# Revit family: Ceiling Tiles - Tegular and Square
name_source: partatom
category: Specialty Equipment
units: mm (PartAtom-declared; Revit-internal decimal feet)

## family parameters
Always vertical = No
Cut with Voids When Loaded = No
Enable Cutting in Views = Yes
Maintain Annotation Orientation = No
OmniClass Number = 23.35.00.00
OmniClass Title = Covering, Cladding, and Finishes
Part Type = Normal
Room Calculation Point = No
Round Connector Dimension = Use Diameter
Shared = No
Work Plane-Based = Yes

## types (168) — shared parameters
Acoustics - NRC = Sound absorption varies from NRC 0.45 to 0.95 based on installation method used when tested per ASTM C423.
Assembly Code = C30
Default Elevation = 4' - 0"
Description = Acoustic Panels
Fire Rating = ASTM E84 - Class A
Manufacturer = Acoustical Surfaces, Inc.
Material = Envirocoustic Wood Wool
Model = Envirocoustic Wood Wool
Recycled Content Percentage = 0%
Type Comments = Acoustic Panels
URL = https://www.acousticalsurfaces.com
Width = 2' - 0"

## per-type parameters (varying)
| type | A | Backer | Backer Options | Backer Thickness | Edge Option | Finish | Length | T | Thickness Options | ‍      0. SoundTex Backer | ‍      0. Thickness 5/8" (only for Square edge) | ‍      1. 1" CFAB Backer | ‍      1. Thickness 1" | ‍      2. 2" CFAB Backer | ‍      2. Thickness 1-3/8" | ‍      3. Thickness 2" | ‍     1. Tegular | ‍     2. Square |
| 2" Square 2x4 Custom Painted With 2” CFAB Backer | 0' - 2" | Yes | 2 | 0' - 2" | 2 | Paint - Acoustical-Surfaces - Custom Painted | 4' - 0" | 0' - 2" | 3 | No | No | No | No | Yes | No | Yes | No | Yes |
| 2" Square 2x2 Custom Painted With 2” CFAB Backer | 0' - 2" | Yes | 2 | 0' - 2" | 2 | Paint - Acoustical-Surfaces - Custom Painted | 2' - 0" | 0' - 2" | 3 | No | No | No | No | Yes | No | Yes | No | Yes |
| 2" Square 2x4 Custom Painted With 1” CFAB Backer | 0' - 1" | Yes | 1 | 0' - 1" | 2 | Paint - Acoustical-Surfaces - Custom Painted | 4' - 0" | 0' - 2" | 3 | No | No | Yes | No | No | No | Yes | No | Yes |
| 2" Square 2x2 Custom Painted With 1” CFAB Backer | 0' - 1" | Yes | 1 | 0' - 1" | 2 | Paint - Acoustical-Surfaces - Custom Painted | 2' - 0" | 0' - 2" | 3 | No | No | Yes | No | No | No | Yes | No | Yes |
| 2" Square 2x4 Custom Painted With Backer 1/16" | 0' - 0" | Yes | 0 | 0' - 0" | 2 | Paint - Acoustical-Surfaces - Custom Painted | 4' - 0" | 0' - 2" | 3 | Yes | No | No | No | No | No | Yes | No | Yes |
| 2" Square 2x2 Custom Painted With Backer 1/16" | 0' - 0" | Yes | 0 | 0' - 0" | 2 | Paint - Acoustical-Surfaces - Custom Painted | 2' - 0" | 0' - 2" | 3 | Yes | No | No | No | No | No | Yes | No | Yes |
| 2" Square 2x4 Custom Painted | 0' - 0" | No | 0 | 0' - 0" | 2 | Paint - Acoustical-Surfaces - Custom Painted | 4' - 0" | 0' - 2" | 3 | Yes | No | No | No | No | No | Yes | No | Yes |
| 2" Square 2x2 Custom Painted | 0' - 0" | No | 0 | 0' - 0" | 2 | Paint - Acoustical-Surfaces - Custom Painted | 2' - 0" | 0' - 2" | 3 | Yes | No | No | No | No | No | Yes | No | Yes |
| 2" Square 2x4 Primed White With 2” CFAB Backer | 0' - 2" | Yes | 2 | 0' - 2" | 2 | Paint - Acoustical-Surfaces - Primed White | 4' - 0" | 0' - 2" | 3 | No | No | No | No | Yes | No | Yes | No | Yes |
| 2" Square 2x2 Primed White With 2” CFAB Backer | 0' - 2" | Yes | 2 | 0' - 2" | 2 | Paint - Acoustical-Surfaces - Primed White | 2' - 0" | 0' - 2" | 3 | No | No | No | No | Yes | No | Yes | No | Yes |
| 2" Square 2x4 Primed White With 1” CFAB Backer | 0' - 1" | Yes | 1 | 0' - 1" | 2 | Paint - Acoustical-Surfaces - Primed White | 4' - 0" | 0' - 2" | 3 | No | No | Yes | No | No | No | Yes | No | Yes |
| 2" Square 2x2 Primed White With 1” CFAB Backer | 0' - 1" | Yes | 1 | 0' - 1" | 2 | Paint - Acoustical-Surfaces - Primed White | 2' - 0" | 0' - 2" | 3 | No | No | Yes | No | No | No | Yes | No | Yes |
| 2" Square 2x4 Primed White With Backer 1/16" | 0' - 0" | Yes | 0 | 0' - 0" | 2 | Paint - Acoustical-Surfaces - Primed White | 4' - 0" | 0' - 2" | 3 | Yes | No | No | No | No | No | Yes | No | Yes |
| 2" Square 2x2 Primed White With Backer 1/16" | 0' - 0" | Yes | 0 | 0' - 0" | 2 | Paint - Acoustical-Surfaces - Primed White | 2' - 0" | 0' - 2" | 3 | Yes | No | No | No | No | No | Yes | No | Yes |
| 2" Square 2x4 Primed White | 0' - 0" | No | 0 | 0' - 0" | 2 | Paint - Acoustical-Surfaces - Primed White | 4' - 0" | 0' - 2" | 3 | Yes | No | No | No | No | No | Yes | No | Yes |
| 2" Square 2x2 Primed White | 0' - 0" | No | 0 | 0' - 0" | 2 | Paint - Acoustical-Surfaces - Primed White | 2' - 0" | 0' - 2" | 3 | Yes | No | No | No | No | No | Yes | No | Yes |
| 2" Square 2x4 Primed Clear With 2” CFAB Backer | 0' - 2" | Yes | 2 | 0' - 2" | 2 | Paint - Acoustical-Surfaces - Primed Clear | 4' - 0" | 0' - 2" | 3 | No | No | No | No | Yes | No | Yes | No | Yes |
| 2" Square 2x2 Primed Clear With 2” CFAB Backer | 0' - 2" | Yes | 2 | 0' - 2" | 2 | Paint - Acoustical-Surfaces - Primed Clear | 2' - 0" | 0' - 2" | 3 | No | No | No | No | Yes | No | Yes | No | Yes |
| 2" Square 2x4 Primed Clear With 1” CFAB Backer | 0' - 1" | Yes | 1 | 0' - 1" | 2 | Paint - Acoustical-Surfaces - Primed Clear | 4' - 0" | 0' - 2" | 3 | No | No | Yes | No | No | No | Yes | No | Yes |
| 2" Square 2x2 Primed Clear With 1” CFAB Backer | 0' - 1" | Yes | 1 | 0' - 1" | 2 | Paint - Acoustical-Surfaces - Primed Clear | 2' - 0" | 0' - 2" | 3 | No | No | Yes | No | No | No | Yes | No | Yes |
| 2" Square 2x4 Primed Clear With Backer 1/16" | 0' - 0" | Yes | 0 | 0' - 0" | 2 | Paint - Acoustical-Surfaces - Primed Clear | 4' - 0" | 0' - 2" | 3 | Yes | No | No | No | No | No | Yes | No | Yes |
| 2" Square 2x2 Primed Clear With Backer 1/16" | 0' - 0" | Yes | 0 | 0' - 0" | 2 | Paint - Acoustical-Surfaces - Primed Clear | 2' - 0" | 0' - 2" | 3 | Yes | No | No | No | No | No | Yes | No | Yes |
| 2" Square 2x4 Primed Clear | 0' - 0" | No | 0 | 0' - 0" | 2 | Paint - Acoustical-Surfaces - Primed Clear | 4' - 0" | 0' - 2" | 3 | Yes | No | No | No | No | No | Yes | No | Yes |
| 2" Square 2x2 Primed Clear | 0' - 0" | No | 0 | 0' - 0" | 2 | Paint - Acoustical-Surfaces - Primed Clear | 2' - 0" | 0' - 2" | 3 | Yes | No | No | No | No | No | Yes | No | Yes |
| 1-3/8" Square 2x4 Custom Painted With 2” CFAB Backer | 0' - 2" | Yes | 2 | 0' - 2" | 2 | Paint - Acoustical-Surfaces - Custom Painted | 4' - 0" | 0' - 1 1/2" | 2 | No | No | No | No | Yes | Yes | No | No | Yes |
| 1-3/8" Square 2x2 Custom Painted With 2” CFAB Backer | 0' - 2" | Yes | 2 | 0' - 2" | 2 | Paint - Acoustical-Surfaces - Custom Painted | 2' - 0" | 0' - 1 1/2" | 2 | No | No | No | No | Yes | Yes | No | No | Yes |
| 1-3/8" Square 2x4 Custom Painted With 1” CFAB Backer | 0' - 1" | Yes | 1 | 0' - 1" | 2 | Paint - Acoustical-Surfaces - Custom Painted | 4' - 0" | 0' - 1 1/2" | 2 | No | No | Yes | No | No | Yes | No | No | Yes |
| 1-3/8" Square 2x2 Custom Painted With 1” CFAB Backer | 0' - 1" | Yes | 1 | 0' - 1" | 2 | Paint - Acoustical-Surfaces - Custom Painted | 2' - 0" | 0' - 1 1/2" | 2 | No | No | Yes | No | No | Yes | No | No | Yes |
| 1-3/8" Square 2x4 Custom Painted With Backer 1/16" | 0' - 0" | Yes | 0 | 0' - 0" | 2 | Paint - Acoustical-Surfaces - Custom Painted | 4' - 0" | 0' - 1 1/2" | 2 | Yes | No | No | No | No | Yes | No | No | Yes |
| 1-3/8" Square 2x2 Custom Painted With Backer 1/16" | 0' - 0" | Yes | 0 | 0' - 0" | 2 | Paint - Acoustical-Surfaces - Custom Painted | 2' - 0" | 0' - 1 1/2" | 2 | Yes | No | No | No | No | Yes | No | No | Yes |
| 1-3/8" Square 2x4 Custom Painted | 0' - 0" | No | 0 | 0' - 0" | 2 | Paint - Acoustical-Surfaces - Custom Painted | 4' - 0" | 0' - 1 1/2" | 2 | Yes | No | No | No | No | Yes | No | No | Yes |
| 1-3/8" Square 2x2 Custom Painted | 0' - 0" | No | 0 | 0' - 0" | 2 | Paint - Acoustical-Surfaces - Custom Painted | 2' - 0" | 0' - 1 1/2" | 2 | Yes | No | No | No | No | Yes | No | No | Yes |
| 1-3/8" Square 2x4 Primed White With 2” CFAB Backer | 0' - 2" | Yes | 2 | 0' - 2" | 2 | Paint - Acoustical-Surfaces - Primed White | 4' - 0" | 0' - 1 1/2" | 2 | No | No | No | No | Yes | Yes | No | No | Yes |
| 1-3/8" Square 2x2 Primed White With 2” CFAB Backer | 0' - 2" | Yes | 2 | 0' - 2" | 2 | Paint - Acoustical-Surfaces - Primed White | 2' - 0" | 0' - 1 1/2" | 2 | No | No | No | No | Yes | Yes | No | No | Yes |
| 1-3/8" Square 2x4 Primed White With 1” CFAB Backer | 0' - 1" | Yes | 1 | 0' - 1" | 2 | Paint - Acoustical-Surfaces - Primed White | 4' - 0" | 0' - 1 1/2" | 2 | No | No | Yes | No | No | Yes | No | No | Yes |
| 1-3/8" Square 2x2 Primed White With 1” CFAB Backer | 0' - 1" | Yes | 1 | 0' - 1" | 2 | Paint - Acoustical-Surfaces - Primed White | 2' - 0" | 0' - 1 1/2" | 2 | No | No | Yes | No | No | Yes | No | No | Yes |
| 1-3/8" Square 2x4 Primed White With Backer 1/16" | 0' - 0" | Yes | 0 | 0' - 0" | 2 | Paint - Acoustical-Surfaces - Primed White | 4' - 0" | 0' - 1 1/2" | 2 | Yes | No | No | No | No | Yes | No | No | Yes |
| 1-3/8" Square 2x2 Primed White With Backer 1/16" | 0' - 0" | Yes | 0 | 0' - 0" | 2 | Paint - Acoustical-Surfaces - Primed White | 2' - 0" | 0' - 1 1/2" | 2 | Yes | No | No | No | No | Yes | No | No | Yes |
| 1-3/8" Square 2x4 Primed White | 0' - 0" | No | 0 | 0' - 0" | 2 | Paint - Acoustical-Surfaces - Primed White | 4' - 0" | 0' - 1 1/2" | 2 | Yes | No | No | No | No | Yes | No | No | Yes |
| 1-3/8" Square 2x2 Primed White | 0' - 0" | No | 0 | 0' - 0" | 2 | Paint - Acoustical-Surfaces - Primed White | 2' - 0" | 0' - 1 1/2" | 2 | Yes | No | No | No | No | Yes | No | No | Yes |
| 1-3/8" Square 2x4 Primed Clear With 2” CFAB Backer | 0' - 2" | Yes | 2 | 0' - 2" | 2 | Paint - Acoustical-Surfaces - Primed Clear | 4' - 0" | 0' - 1 1/2" | 2 | No | No | No | No | Yes | Yes | No | No | Yes |
| 1-3/8" Square 2x2 Primed Clear With 2” CFAB Backer | 0' - 2" | Yes | 2 | 0' - 2" | 2 | Paint - Acoustical-Surfaces - Primed Clear | 2' - 0" | 0' - 1 1/2" | 2 | No | No | No | No | Yes | Yes | No | No | Yes |
| 1-3/8" Square 2x4 Primed Clear With 1” CFAB Backer | 0' - 1" | Yes | 1 | 0' - 1" | 2 | Paint - Acoustical-Surfaces - Primed Clear | 4' - 0" | 0' - 1 1/2" | 2 | No | No | Yes | No | No | Yes | No | No | Yes |
| 1-3/8" Square 2x2 Primed Clear With 1” CFAB Backer | 0' - 1" | Yes | 1 | 0' - 1" | 2 | Paint - Acoustical-Surfaces - Primed Clear | 2' - 0" | 0' - 1 1/2" | 2 | No | No | Yes | No | No | Yes | No | No | Yes |
| 1-3/8" Square 2x4 Primed Clear With Backer 1/16" | 0' - 0" | Yes | 0 | 0' - 0" | 2 | Paint - Acoustical-Surfaces - Primed Clear | 4' - 0" | 0' - 1 1/2" | 2 | Yes | No | No | No | No | Yes | No | No | Yes |
| 1-3/8" Square 2x2 Primed Clear With Backer 1/16" | 0' - 0" | Yes | 0 | 0' - 0" | 2 | Paint - Acoustical-Surfaces - Primed Clear | 2' - 0" | 0' - 1 1/2" | 2 | Yes | No | No | No | No | Yes | No | No | Yes |
| 1-3/8" Square 2x4 Primed Clear | 0' - 0" | No | 0 | 0' - 0" | 2 | Paint - Acoustical-Surfaces - Primed Clear | 4' - 0" | 0' - 1 1/2" | 2 | Yes | No | No | No | No | Yes | No | No | Yes |
| 1-3/8" Square 2x2 Primed Clear | 0' - 0" | No | 0 | 0' - 0" | 2 | Paint - Acoustical-Surfaces - Primed Clear | 2' - 0" | 0' - 1 1/2" | 2 | Yes | No | No | No | No | Yes | No | No | Yes |
| 1" Square 2x4 Custom Painted With 2” CFAB Backer | 0' - 2" | Yes | 2 | 0' - 2" | 2 | Paint - Acoustical-Surfaces - Custom Painted | 4' - 0" | 0' - 1" | 1 | No | No | No | Yes | Yes | No | No | No | Yes |
| 1" Square 2x2 Custom Painted With 2” CFAB Backer | 0' - 2" | Yes | 2 | 0' - 2" | 2 | Paint - Acoustical-Surfaces - Custom Painted | 2' - 0" | 0' - 1" | 1 | No | No | No | Yes | Yes | No | No | No | Yes |
| 1" Square 2x4 Custom Painted With 1” CFAB Backer | 0' - 1" | Yes | 1 | 0' - 1" | 2 | Paint - Acoustical-Surfaces - Custom Painted | 4' - 0" | 0' - 1" | 1 | No | No | Yes | Yes | No | No | No | No | Yes |
| 1" Square 2x2 Custom Painted With 1” CFAB Backer | 0' - 1" | Yes | 1 | 0' - 1" | 2 | Paint - Acoustical-Surfaces - Custom Painted | 2' - 0" | 0' - 1" | 1 | No | No | Yes | Yes | No | No | No | No | Yes |
| 1" Square 2x4 Custom Painted With Backer 1/16" | 0' - 0" | Yes | 0 | 0' - 0" | 2 | Paint - Acoustical-Surfaces - Custom Painted | 4' - 0" | 0' - 1" | 1 | Yes | No | No | Yes | No | No | No | No | Yes |
| 1" Square 2x2 Custom Painted With Backer 1/16" | 0' - 0" | Yes | 0 | 0' - 0" | 2 | Paint - Acoustical-Surfaces - Custom Painted | 2' - 0" | 0' - 1" | 1 | Yes | No | No | Yes | No | No | No | No | Yes |
| 1" Square 2x4 Custom Painted | 0' - 0" | No | 0 | 0' - 0" | 2 | Paint - Acoustical-Surfaces - Custom Painted | 4' - 0" | 0' - 1" | 1 | Yes | No | No | Yes | No | No | No | No | Yes |
| 1" Square 2x2 Custom Painted | 0' - 0" | No | 0 | 0' - 0" | 2 | Paint - Acoustical-Surfaces - Custom Painted | 2' - 0" | 0' - 1" | 1 | Yes | No | No | Yes | No | No | No | No | Yes |
| 1" Square 2x4 Primed White With 2” CFAB Backer | 0' - 2" | Yes | 2 | 0' - 2" | 2 | Paint - Acoustical-Surfaces - Primed White | 4' - 0" | 0' - 1" | 1 | No | No | No | Yes | Yes | No | No | No | Yes |
| 1" Square 2x2 Primed White With 2” CFAB Backer | 0' - 2" | Yes | 2 | 0' - 2" | 2 | Paint - Acoustical-Surfaces - Primed White | 2' - 0" | 0' - 1" | 1 | No | No | No | Yes | Yes | No | No | No | Yes |
| 1" Square 2x4 Primed White With 1” CFAB Backer | 0' - 1" | Yes | 1 | 0' - 1" | 2 | Paint - Acoustical-Surfaces - Primed White | 4' - 0" | 0' - 1" | 1 | No | No | Yes | Yes | No | No | No | No | Yes |
| 1" Square 2x2 Primed White With 1” CFAB Backer | 0' - 1" | Yes | 1 | 0' - 1" | 2 | Paint - Acoustical-Surfaces - Primed White | 2' - 0" | 0' - 1" | 1 | No | No | Yes | Yes | No | No | No | No | Yes |
| 1" Square 2x4 Primed White With Backer 1/16" | 0' - 0" | Yes | 0 | 0' - 0" | 2 | Paint - Acoustical-Surfaces - Primed White | 4' - 0" | 0' - 1" | 1 | Yes | No | No | Yes | No | No | No | No | Yes |
| 1" Square 2x2 Primed White With Backer 1/16" | 0' - 0" | Yes | 0 | 0' - 0" | 2 | Paint - Acoustical-Surfaces - Primed White | 2' - 0" | 0' - 1" | 1 | Yes | No | No | Yes | No | No | No | No | Yes |
| 1" Square 2x4 Primed White | 0' - 0" | No | 0 | 0' - 0" | 2 | Paint - Acoustical-Surfaces - Primed White | 4' - 0" | 0' - 1" | 1 | Yes | No | No | Yes | No | No | No | No | Yes |
| 1" Square 2x2 Primed White | 0' - 0" | No | 0 | 0' - 0" | 2 | Paint - Acoustical-Surfaces - Primed White | 2' - 0" | 0' - 1" | 1 | Yes | No | No | Yes | No | No | No | No | Yes |
| 1" Square 2x4 Primed Clear With 2” CFAB Backer | 0' - 2" | Yes | 2 | 0' - 2" | 2 | Paint - Acoustical-Surfaces - Primed Clear | 4' - 0" | 0' - 1" | 1 | No | No | No | Yes | Yes | No | No | No | Yes |
| 1" Square 2x2 Primed Clear With 2” CFAB Backer | 0' - 2" | Yes | 2 | 0' - 2" | 2 | Paint - Acoustical-Surfaces - Primed Clear | 2' - 0" | 0' - 1" | 1 | No | No | No | Yes | Yes | No | No | No | Yes |
| 1" Square 2x4 Primed Clear With 1” CFAB Backer | 0' - 1" | Yes | 1 | 0' - 1" | 2 | Paint - Acoustical-Surfaces - Primed Clear | 4' - 0" | 0' - 1" | 1 | No | No | Yes | Yes | No | No | No | No | Yes |
| 1" Square 2x2 Primed Clear With 1” CFAB Backer | 0' - 1" | Yes | 1 | 0' - 1" | 2 | Paint - Acoustical-Surfaces - Primed Clear | 2' - 0" | 0' - 1" | 1 | No | No | Yes | Yes | No | No | No | No | Yes |
| 1" Square 2x4 Primed Clear With Backer 1/16" | 0' - 0" | Yes | 0 | 0' - 0" | 2 | Paint - Acoustical-Surfaces - Primed Clear | 4' - 0" | 0' - 1" | 1 | Yes | No | No | Yes | No | No | No | No | Yes |
| 1" Square 2x2 Primed Clear With Backer 1/16" | 0' - 0" | Yes | 0 | 0' - 0" | 2 | Paint - Acoustical-Surfaces - Primed Clear | 2' - 0" | 0' - 1" | 1 | Yes | No | No | Yes | No | No | No | No | Yes |
| 1" Square 2x4 Primed Clear | 0' - 0" | No | 0 | 0' - 0" | 2 | Paint - Acoustical-Surfaces - Primed Clear | 4' - 0" | 0' - 1" | 1 | Yes | No | No | Yes | No | No | No | No | Yes |
| 1" Square 2x2 Primed Clear | 0' - 0" | No | 0 | 0' - 0" | 2 | Paint - Acoustical-Surfaces - Primed Clear | 2' - 0" | 0' - 1" | 1 | Yes | No | No | Yes | No | No | No | No | Yes |
| 2" Tegular 2x4 Custom Painted With 2” CFAB Backer | 0' - 2" | Yes | 2 | 0' - 2" | 1 | Paint - Acoustical-Surfaces - Custom Painted | 4' - 0" | 0' - 2" | 3 | No | No | No | No | Yes | No | Yes | Yes | No |
| 2" Tegular 2x2 Custom Painted With 2” CFAB Backer | 0' - 2" | Yes | 2 | 0' - 2" | 1 | Paint - Acoustical-Surfaces - Custom Painted | 2' - 0" | 0' - 2" | 3 | No | No | No | No | Yes | No | Yes | Yes | No |
| 2" Tegular 2x4 Custom Painted With 1” CFAB Backer | 0' - 1" | Yes | 1 | 0' - 1" | 1 | Paint - Acoustical-Surfaces - Custom Painted | 4' - 0" | 0' - 2" | 3 | No | No | Yes | No | No | No | Yes | Yes | No |
| 2" Tegular 2x2 Custom Painted With 1” CFAB Backer | 0' - 1" | Yes | 1 | 0' - 1" | 1 | Paint - Acoustical-Surfaces - Custom Painted | 2' - 0" | 0' - 2" | 3 | No | No | Yes | No | No | No | Yes | Yes | No |
| 2" Tegular 2x4 Custom Painted With Backer 1/16" | 0' - 0" | Yes | 0 | 0' - 0" | 1 | Paint - Acoustical-Surfaces - Custom Painted | 4' - 0" | 0' - 2" | 3 | Yes | No | No | No | No | No | Yes | Yes | No |
| 2" Tegular 2x2 Custom Painted With Backer 1/16" | 0' - 0" | Yes | 0 | 0' - 0" | 1 | Paint - Acoustical-Surfaces - Custom Painted | 2' - 0" | 0' - 2" | 3 | Yes | No | No | No | No | No | Yes | Yes | No |
| 2" Tegular 2x4 Custom Painted | 0' - 0" | No | 0 | 0' - 0" | 1 | Paint - Acoustical-Surfaces - Custom Painted | 4' - 0" | 0' - 2" | 3 | Yes | No | No | No | No | No | Yes | Yes | No |
| 2" Tegular 2x2 Custom Painted | 0' - 0" | No | 0 | 0' - 0" | 1 | Paint - Acoustical-Surfaces - Custom Painted | 2' - 0" | 0' - 2" | 3 | Yes | No | No | No | No | No | Yes | Yes | No |
| 2" Tegular 2x4 Primed White With 2” CFAB Backer | 0' - 2" | Yes | 2 | 0' - 2" | 1 | Paint - Acoustical-Surfaces - Primed White | 4' - 0" | 0' - 2" | 3 | No | No | No | No | Yes | No | Yes | Yes | No |
| 2" Tegular 2x2 Primed White With 2” CFAB Backer | 0' - 2" | Yes | 2 | 0' - 2" | 1 | Paint - Acoustical-Surfaces - Primed White | 2' - 0" | 0' - 2" | 3 | No | No | No | No | Yes | No | Yes | Yes | No |
| 2" Tegular 2x4 Primed White With 1” CFAB Backer | 0' - 1" | Yes | 1 | 0' - 1" | 1 | Paint - Acoustical-Surfaces - Primed White | 4' - 0" | 0' - 2" | 3 | No | No | Yes | No | No | No | Yes | Yes | No |
| 2" Tegular 2x2 Primed White With 1” CFAB Backer | 0' - 1" | Yes | 1 | 0' - 1" | 1 | Paint - Acoustical-Surfaces - Primed White | 2' - 0" | 0' - 2" | 3 | No | No | Yes | No | No | No | Yes | Yes | No |
| 2" Tegular 2x4 Primed White With Backer 1/16" | 0' - 0" | Yes | 0 | 0' - 0" | 1 | Paint - Acoustical-Surfaces - Primed White | 4' - 0" | 0' - 2" | 3 | Yes | No | No | No | No | No | Yes | Yes | No |
| 2" Tegular 2x2 Primed White With Backer 1/16" | 0' - 0" | Yes | 0 | 0' - 0" | 1 | Paint - Acoustical-Surfaces - Primed White | 2' - 0" | 0' - 2" | 3 | Yes | No | No | No | No | No | Yes | Yes | No |
| 2" Tegular 2x4 Primed White | 0' - 0" | No | 0 | 0' - 0" | 1 | Paint - Acoustical-Surfaces - Primed White | 4' - 0" | 0' - 2" | 3 | Yes | No | No | No | No | No | Yes | Yes | No |
| 2" Tegular 2x2 Primed White | 0' - 0" | No | 0 | 0' - 0" | 1 | Paint - Acoustical-Surfaces - Primed White | 2' - 0" | 0' - 2" | 3 | Yes | No | No | No | No | No | Yes | Yes | No |
| 2" Tegular 2x4 Primed Clear With 2” CFAB Backer | 0' - 2" | Yes | 2 | 0' - 2" | 1 | Paint - Acoustical-Surfaces - Primed Clear | 4' - 0" | 0' - 2" | 3 | No | No | No | No | Yes | No | Yes | Yes | No |
| 2" Tegular 2x2 Primed Clear With 2” CFAB Backer | 0' - 2" | Yes | 2 | 0' - 2" | 1 | Paint - Acoustical-Surfaces - Primed Clear | 2' - 0" | 0' - 2" | 3 | No | No | No | No | Yes | No | Yes | Yes | No |
| 2" Tegular 2x4 Primed Clear With 1” CFAB Backer | 0' - 1" | Yes | 1 | 0' - 1" | 1 | Paint - Acoustical-Surfaces - Primed Clear | 4' - 0" | 0' - 2" | 3 | No | No | Yes | No | No | No | Yes | Yes | No |
| 2" Tegular 2x2 Primed Clear With 1” CFAB Backer | 0' - 1" | Yes | 1 | 0' - 1" | 1 | Paint - Acoustical-Surfaces - Primed Clear | 2' - 0" | 0' - 2" | 3 | No | No | Yes | No | No | No | Yes | Yes | No |
| 2" Tegular 2x4 Primed Clear With Backer 1/16" | 0' - 0" | Yes | 0 | 0' - 0" | 1 | Paint - Acoustical-Surfaces - Primed Clear | 4' - 0" | 0' - 2" | 3 | Yes | No | No | No | No | No | Yes | Yes | No |
| 2" Tegular 2x2 Primed Clear With Backer 1/16" | 0' - 0" | Yes | 0 | 0' - 0" | 1 | Paint - Acoustical-Surfaces - Primed Clear | 2' - 0" | 0' - 2" | 3 | Yes | No | No | No | No | No | Yes | Yes | No |
| 2" Tegular 2x4 Primed Clear | 0' - 0" | No | 0 | 0' - 0" | 1 | Paint - Acoustical-Surfaces - Primed Clear | 4' - 0" | 0' - 2" | 3 | Yes | No | No | No | No | No | Yes | Yes | No |
| 2" Tegular 2x2 Primed Clear | 0' - 0" | No | 0 | 0' - 0" | 1 | Paint - Acoustical-Surfaces - Primed Clear | 2' - 0" | 0' - 2" | 3 | Yes | No | No | No | No | No | Yes | Yes | No |
| 1-3/8" Tegular 2x4 Custom Painted With 2” CFAB Backer | 0' - 2" | Yes | 2 | 0' - 2" | 1 | Paint - Acoustical-Surfaces - Custom Painted | 4' - 0" | 0' - 1 1/2" | 2 | No | No | No | No | Yes | Yes | No | Yes | No |
| 1-3/8" Tegular 2x2 Custom Painted With 2” CFAB Backer | 0' - 2" | Yes | 2 | 0' - 2" | 1 | Paint - Acoustical-Surfaces - Custom Painted | 2' - 0" | 0' - 1 1/2" | 2 | No | No | No | No | Yes | Yes | No | Yes | No |
| 1-3/8" Tegular 2x4 Custom Painted With 1” CFAB Backer | 0' - 1" | Yes | 1 | 0' - 1" | 1 | Paint - Acoustical-Surfaces - Custom Painted | 4' - 0" | 0' - 1 1/2" | 2 | No | No | Yes | No | No | Yes | No | Yes | No |
| 1-3/8" Tegular 2x2 Custom Painted With 1” CFAB Backer | 0' - 1" | Yes | 1 | 0' - 1" | 1 | Paint - Acoustical-Surfaces - Custom Painted | 2' - 0" | 0' - 1 1/2" | 2 | No | No | Yes | No | No | Yes | No | Yes | No |
| 1-3/8" Tegular 2x4 Custom Painted With Backer 1/16" | 0' - 0" | Yes | 0 | 0' - 0" | 1 | Paint - Acoustical-Surfaces - Custom Painted | 4' - 0" | 0' - 1 1/2" | 2 | Yes | No | No | No | No | Yes | No | Yes | No |
| 1-3/8" Tegular 2x2 Custom Painted With Backer 1/16" | 0' - 0" | Yes | 0 | 0' - 0" | 1 | Paint - Acoustical-Surfaces - Custom Painted | 2' - 0" | 0' - 1 1/2" | 2 | Yes | No | No | No | No | Yes | No | Yes | No |
| 1-3/8" Tegular 2x4 Custom Painted | 0' - 0" | No | 0 | 0' - 0" | 1 | Paint - Acoustical-Surfaces - Custom Painted | 4' - 0" | 0' - 1 1/2" | 2 | Yes | No | No | No | No | Yes | No | Yes | No |
| 1-3/8" Tegular 2x2 Custom Painted | 0' - 0" | No | 0 | 0' - 0" | 1 | Paint - Acoustical-Surfaces - Custom Painted | 2' - 0" | 0' - 1 1/2" | 2 | Yes | No | No | No | No | Yes | No | Yes | No |
| 1-3/8" Tegular 2x4 Primed White With 2” CFAB Backer | 0' - 2" | Yes | 2 | 0' - 2" | 1 | Paint - Acoustical-Surfaces - Primed White | 4' - 0" | 0' - 1 1/2" | 2 | No | No | No | No | Yes | Yes | No | Yes | No |
| 1-3/8" Tegular 2x2 Primed White With 2” CFAB Backer | 0' - 2" | Yes | 2 | 0' - 2" | 1 | Paint - Acoustical-Surfaces - Primed White | 2' - 0" | 0' - 1 1/2" | 2 | No | No | No | No | Yes | Yes | No | Yes | No |
| 1-3/8" Tegular 2x4 Primed White With 1” CFAB Backer | 0' - 1" | Yes | 1 | 0' - 1" | 1 | Paint - Acoustical-Surfaces - Primed White | 4' - 0" | 0' - 1 1/2" | 2 | No | No | Yes | No | No | Yes | No | Yes | No |
| 1-3/8" Tegular 2x2 Primed White With 1” CFAB Backer | 0' - 1" | Yes | 1 | 0' - 1" | 1 | Paint - Acoustical-Surfaces - Primed White | 2' - 0" | 0' - 1 1/2" | 2 | No | No | Yes | No | No | Yes | No | Yes | No |
| 1-3/8" Tegular 2x4 Primed White With Backer 1/16" | 0' - 0" | Yes | 0 | 0' - 0" | 1 | Paint - Acoustical-Surfaces - Primed White | 4' - 0" | 0' - 1 1/2" | 2 | Yes | No | No | No | No | Yes | No | Yes | No |
| 1-3/8" Tegular 2x2 Primed White With Backer 1/16" | 0' - 0" | Yes | 0 | 0' - 0" | 1 | Paint - Acoustical-Surfaces - Primed White | 2' - 0" | 0' - 1 1/2" | 2 | Yes | No | No | No | No | Yes | No | Yes | No |
| 1-3/8" Tegular 2x4 Primed White | 0' - 0" | No | 0 | 0' - 0" | 1 | Paint - Acoustical-Surfaces - Primed White | 4' - 0" | 0' - 1 1/2" | 2 | Yes | No | No | No | No | Yes | No | Yes | No |
| 1-3/8" Tegular 2x2 Primed White | 0' - 0" | No | 0 | 0' - 0" | 1 | Paint - Acoustical-Surfaces - Primed White | 2' - 0" | 0' - 1 1/2" | 2 | Yes | No | No | No | No | Yes | No | Yes | No |
| 1-3/8" Tegular 2x4 Primed Clear With 2” CFAB Backer | 0' - 2" | Yes | 2 | 0' - 2" | 1 | Paint - Acoustical-Surfaces - Primed Clear | 4' - 0" | 0' - 1 1/2" | 2 | No | No | No | No | Yes | Yes | No | Yes | No |
| 1-3/8" Tegular 2x2 Primed Clear With 2” CFAB Backer | 0' - 2" | Yes | 2 | 0' - 2" | 1 | Paint - Acoustical-Surfaces - Primed Clear | 2' - 0" | 0' - 1 1/2" | 2 | No | No | No | No | Yes | Yes | No | Yes | No |
| 1-3/8" Tegular 2x4 Primed Clear With 1” CFAB Backer | 0' - 1" | Yes | 1 | 0' - 1" | 1 | Paint - Acoustical-Surfaces - Primed Clear | 4' - 0" | 0' - 1 1/2" | 2 | No | No | Yes | No | No | Yes | No | Yes | No |
| 1-3/8" Tegular 2x2 Primed Clear With 1” CFAB Backer | 0' - 1" | Yes | 1 | 0' - 1" | 1 | Paint - Acoustical-Surfaces - Primed Clear | 2' - 0" | 0' - 1 1/2" | 2 | No | No | Yes | No | No | Yes | No | Yes | No |
| 1-3/8" Tegular 2x4 Primed Clear With Backer 1/16" | 0' - 0" | Yes | 0 | 0' - 0" | 1 | Paint - Acoustical-Surfaces - Primed Clear | 4' - 0" | 0' - 1 1/2" | 2 | Yes | No | No | No | No | Yes | No | Yes | No |
| 1-3/8" Tegular 2x2 Primed Clear With Backer 1/16" | 0' - 0" | Yes | 0 | 0' - 0" | 1 | Paint - Acoustical-Surfaces - Primed Clear | 2' - 0" | 0' - 1 1/2" | 2 | Yes | No | No | No | No | Yes | No | Yes | No |
| 1-3/8" Tegular 2x4 Primed Clear | 0' - 0" | No | 0 | 0' - 0" | 1 | Paint - Acoustical-Surfaces - Primed Clear | 4' - 0" | 0' - 1 1/2" | 2 | Yes | No | No | No | No | Yes | No | Yes | No |
| 1-3/8" Tegular 2x2 Primed Clear | 0' - 0" | No | 0 | 0' - 0" | 1 | Paint - Acoustical-Surfaces - Primed Clear | 2' - 0" | 0' - 1 1/2" | 2 | Yes | No | No | No | No | Yes | No | Yes | No |
| 5/8" Square 2x4 Custom Painted With 2” CFAB Backer | 0' - 2" | Yes | 2 | 0' - 2" | 2 | Paint - Acoustical-Surfaces - Custom Painted | 4' - 0" | 0' - 0 1/2" | 0 | No | Yes | No | No | Yes | No | No | No | Yes |
| 5/8" Square 2x4 Primed White With 2” CFAB Backer | 0' - 2" | Yes | 2 | 0' - 2" | 2 | Paint - Acoustical-Surfaces - Primed White | 4' - 0" | 0' - 0 1/2" | 0 | No | Yes | No | No | Yes | No | No | No | Yes |
| 5/8" Square 2x4 Primed Clear With 2” CFAB Backer | 0' - 2" | Yes | 2 | 0' - 2" | 2 | Paint - Acoustical-Surfaces - Primed Clear | 4' - 0" | 0' - 0 1/2" | 0 | No | Yes | No | No | Yes | No | No | No | Yes |
| 1" Tegular 2x4 Custom Painted With 2” CFAB Backer | 0' - 2" | Yes | 2 | 0' - 2" | 1 | Paint - Acoustical-Surfaces - Custom Painted | 4' - 0" | 0' - 1" | 1 | No | No | No | Yes | Yes | No | No | Yes | No |
| 1" Tegular 2x4 Primed White With 2” CFAB Backer | 0' - 2" | Yes | 2 | 0' - 2" | 1 | Paint - Acoustical-Surfaces - Primed White | 4' - 0" | 0' - 1" | 1 | No | No | No | Yes | Yes | No | No | Yes | No |
| 1" Tegular 2x4 Primed Clear With 2” CFAB Backer | 0' - 2" | Yes | 2 | 0' - 2" | 1 | Paint - Acoustical-Surfaces - Primed Clear | 4' - 0" | 0' - 1" | 1 | No | No | No | Yes | Yes | No | No | Yes | No |
| 5/8" Square 2x2 Custom Painted With 2” CFAB Backer | 0' - 2" | Yes | 2 | 0' - 2" | 2 | Paint - Acoustical-Surfaces - Custom Painted | 2' - 0" | 0' - 0 1/2" | 0 | No | Yes | No | No | Yes | No | No | No | Yes |
| 5/8" Square 2x2 Primed White With 2” CFAB Backer | 0' - 2" | Yes | 2 | 0' - 2" | 2 | Paint - Acoustical-Surfaces - Primed White | 2' - 0" | 0' - 0 1/2" | 0 | No | Yes | No | No | Yes | No | No | No | Yes |
| 5/8" Square 2x2 Primed Clear With 2” CFAB Backer | 0' - 2" | Yes | 2 | 0' - 2" | 2 | Paint - Acoustical-Surfaces - Primed Clear | 2' - 0" | 0' - 0 1/2" | 0 | No | Yes | No | No | Yes | No | No | No | Yes |
| 1" Tegular 2x2 Custom Painted With 2” CFAB Backer | 0' - 2" | Yes | 2 | 0' - 2" | 1 | Paint - Acoustical-Surfaces - Custom Painted | 2' - 0" | 0' - 1" | 1 | No | No | No | Yes | Yes | No | No | Yes | No |
| 1" Tegular 2x2 Primed White With 2” CFAB Backer | 0' - 2" | Yes | 2 | 0' - 2" | 1 | Paint - Acoustical-Surfaces - Primed White | 2' - 0" | 0' - 1" | 1 | No | No | No | Yes | Yes | No | No | Yes | No |
| 1" Tegular 2x2 Primed Clear With 2” CFAB Backer | 0' - 2" | Yes | 2 | 0' - 2" | 1 | Paint - Acoustical-Surfaces - Primed Clear | 2' - 0" | 0' - 1" | 1 | No | No | No | Yes | Yes | No | No | Yes | No |
| 5/8" Square 2x4 Custom Painted With 1” CFAB Backer | 0' - 1" | Yes | 1 | 0' - 1" | 2 | Paint - Acoustical-Surfaces - Custom Painted | 4' - 0" | 0' - 0 1/2" | 0 | No | Yes | Yes | No | No | No | No | No | Yes |
| 5/8" Square 2x4 Primed White With 1” CFAB Backer | 0' - 1" | Yes | 1 | 0' - 1" | 2 | Paint - Acoustical-Surfaces - Primed White | 4' - 0" | 0' - 0 1/2" | 0 | No | Yes | Yes | No | No | No | No | No | Yes |
| 5/8" Square 2x4 Primed Clear With 1” CFAB Backer | 0' - 1" | Yes | 1 | 0' - 1" | 2 | Paint - Acoustical-Surfaces - Primed Clear | 4' - 0" | 0' - 0 1/2" | 0 | No | Yes | Yes | No | No | No | No | No | Yes |
| 1" Tegular 2x4 Custom Painted With 1” CFAB Backer | 0' - 1" | Yes | 1 | 0' - 1" | 1 | Paint - Acoustical-Surfaces - Custom Painted | 4' - 0" | 0' - 1" | 1 | No | No | Yes | Yes | No | No | No | Yes | No |
| 1" Tegular 2x4 Primed White With 1” CFAB Backer | 0' - 1" | Yes | 1 | 0' - 1" | 1 | Paint - Acoustical-Surfaces - Primed White | 4' - 0" | 0' - 1" | 1 | No | No | Yes | Yes | No | No | No | Yes | No |
| 1" Tegular 2x4 Primed Clear With 1” CFAB Backer | 0' - 1" | Yes | 1 | 0' - 1" | 1 | Paint - Acoustical-Surfaces - Primed Clear | 4' - 0" | 0' - 1" | 1 | No | No | Yes | Yes | No | No | No | Yes | No |
| 5/8" Square 2x2 Custom Painted With 1” CFAB Backer | 0' - 1" | Yes | 1 | 0' - 1" | 2 | Paint - Acoustical-Surfaces - Custom Painted | 2' - 0" | 0' - 0 1/2" | 0 | No | Yes | Yes | No | No | No | No | No | Yes |
| 5/8" Square 2x2 Primed White With 1” CFAB Backer | 0' - 1" | Yes | 1 | 0' - 1" | 2 | Paint - Acoustical-Surfaces - Primed White | 2' - 0" | 0' - 0 1/2" | 0 | No | Yes | Yes | No | No | No | No | No | Yes |
| 5/8" Square 2x2 Primed Clear With 1” CFAB Backer | 0' - 1" | Yes | 1 | 0' - 1" | 2 | Paint - Acoustical-Surfaces - Primed Clear | 2' - 0" | 0' - 0 1/2" | 0 | No | Yes | Yes | No | No | No | No | No | Yes |
| 1" Tegular 2x2 Custom Painted With 1” CFAB Backer | 0' - 1" | Yes | 1 | 0' - 1" | 1 | Paint - Acoustical-Surfaces - Custom Painted | 2' - 0" | 0' - 1" | 1 | No | No | Yes | Yes | No | No | No | Yes | No |
| 1" Tegular 2x2 Primed White With 1” CFAB Backer | 0' - 1" | Yes | 1 | 0' - 1" | 1 | Paint - Acoustical-Surfaces - Primed White | 2' - 0" | 0' - 1" | 1 | No | No | Yes | Yes | No | No | No | Yes | No |
| 1" Tegular 2x2 Primed Clear With 1” CFAB Backer | 0' - 1" | Yes | 1 | 0' - 1" | 1 | Paint - Acoustical-Surfaces - Primed Clear | 2' - 0" | 0' - 1" | 1 | No | No | Yes | Yes | No | No | No | Yes | No |
| 5/8" Square 2x4 Custom Painted | 0' - 0" | No | 0 | 0' - 0" | 2 | Paint - Acoustical-Surfaces - Custom Painted | 4' - 0" | 0' - 0 1/2" | 0 | Yes | Yes | No | No | No | No | No | No | Yes |
| 5/8" Square 2x2 Custom Painted | 0' - 0" | No | 0 | 0' - 0" | 2 | Paint - Acoustical-Surfaces - Custom Painted | 2' - 0" | 0' - 0 1/2" | 0 | Yes | Yes | No | No | No | No | No | No | Yes |
| 5/8" Square 2x4 Primed White | 0' - 0" | No | 0 | 0' - 0" | 2 | Paint - Acoustical-Surfaces - Primed White | 4' - 0" | 0' - 0 1/2" | 0 | Yes | Yes | No | No | No | No | No | No | Yes |
| 5/8" Square 2x2 Primed White | 0' - 0" | No | 0 | 0' - 0" | 2 | Paint - Acoustical-Surfaces - Primed White | 2' - 0" | 0' - 0 1/2" | 0 | Yes | Yes | No | No | No | No | No | No | Yes |
| 5/8" Square 2x4 Primed Clear | 0' - 0" | No | 0 | 0' - 0" | 2 | Paint - Acoustical-Surfaces - Primed Clear | 4' - 0" | 0' - 0 1/2" | 0 | Yes | Yes | No | No | No | No | No | No | Yes |
| 5/8" Square 2x2 Primed Clear | 0' - 0" | No | 0 | 0' - 0" | 2 | Paint - Acoustical-Surfaces - Primed Clear | 2' - 0" | 0' - 0 1/2" | 0 | Yes | Yes | No | No | No | No | No | No | Yes |
| 5/8" Square 2x4 Custom Painted With Backer 1/16" | 0' - 0" | Yes | 0 | 0' - 0" | 2 | Paint - Acoustical-Surfaces - Custom Painted | 4' - 0" | 0' - 0 1/2" | 0 | Yes | Yes | No | No | No | No | No | No | Yes |
| 5/8" Square 2x2 Custom Painted With Backer 1/16" | 0' - 0" | Yes | 0 | 0' - 0" | 2 | Paint - Acoustical-Surfaces - Custom Painted | 2' - 0" | 0' - 0 1/2" | 0 | Yes | Yes | No | No | No | No | No | No | Yes |
| 5/8" Square 2x4 Primed White With Backer 1/16" | 0' - 0" | Yes | 0 | 0' - 0" | 2 | Paint - Acoustical-Surfaces - Primed White | 4' - 0" | 0' - 0 1/2" | 0 | Yes | Yes | No | No | No | No | No | No | Yes |
| 5/8" Square 2x2 Primed White With Backer 1/16" | 0' - 0" | Yes | 0 | 0' - 0" | 2 | Paint - Acoustical-Surfaces - Primed White | 2' - 0" | 0' - 0 1/2" | 0 | Yes | Yes | No | No | No | No | No | No | Yes |
| 5/8" Square 2x4 Primed Clear With Backer 1/16" | 0' - 0" | Yes | 0 | 0' - 0" | 2 | Paint - Acoustical-Surfaces - Primed Clear | 4' - 0" | 0' - 0 1/2" | 0 | Yes | Yes | No | No | No | No | No | No | Yes |
| 5/8" Square 2x2 Primed Clear With Backer 1/16" | 0' - 0" | Yes | 0 | 0' - 0" | 2 | Paint - Acoustical-Surfaces - Primed Clear | 2' - 0" | 0' - 0 1/2" | 0 | Yes | Yes | No | No | No | No | No | No | Yes |
| 1" Tegular 2x4 Custom Painted | 0' - 0" | No | 0 | 0' - 0" | 1 | Paint - Acoustical-Surfaces - Custom Painted | 4' - 0" | 0' - 1" | 1 | Yes | No | No | Yes | No | No | No | Yes | No |
| 1" Tegular 2x2 Custom Painted | 0' - 0" | No | 0 | 0' - 0" | 1 | Paint - Acoustical-Surfaces - Custom Painted | 2' - 0" | 0' - 1" | 1 | Yes | No | No | Yes | No | No | No | Yes | No |
| 1" Tegular 2x4 Primed White | 0' - 0" | No | 0 | 0' - 0" | 1 | Paint - Acoustical-Surfaces - Primed White | 4' - 0" | 0' - 1" | 1 | Yes | No | No | Yes | No | No | No | Yes | No |
| 1" Tegular 2x2 Primed White | 0' - 0" | No | 0 | 0' - 0" | 1 | Paint - Acoustical-Surfaces - Primed White | 2' - 0" | 0' - 1" | 1 | Yes | No | No | Yes | No | No | No | Yes | No |
| 1" Tegular 2x4 Primed Clear | 0' - 0" | No | 0 | 0' - 0" | 1 | Paint - Acoustical-Surfaces - Primed Clear | 4' - 0" | 0' - 1" | 1 | Yes | No | No | Yes | No | No | No | Yes | No |
| 1" Tegular 2x2 Primed Clear | 0' - 0" | No | 0 | 0' - 0" | 1 | Paint - Acoustical-Surfaces - Primed Clear | 2' - 0" | 0' - 1" | 1 | Yes | No | No | Yes | No | No | No | Yes | No |
| 1" Tegular 2x4 Custom Painted With Backer 1/16" | 0' - 0" | Yes | 0 | 0' - 0" | 1 | Paint - Acoustical-Surfaces - Custom Painted | 4' - 0" | 0' - 1" | 1 | Yes | No | No | Yes | No | No | No | Yes | No |
| 1" Tegular 2x2 Custom Painted With Backer 1/16" | 0' - 0" | Yes | 0 | 0' - 0" | 1 | Paint - Acoustical-Surfaces - Custom Painted | 2' - 0" | 0' - 1" | 1 | Yes | No | No | Yes | No | No | No | Yes | No |
| 1" Tegular 2x4 Primed White With Backer 1/16" | 0' - 0" | Yes | 0 | 0' - 0" | 1 | Paint - Acoustical-Surfaces - Primed White | 4' - 0" | 0' - 1" | 1 | Yes | No | No | Yes | No | No | No | Yes | No |
| 1" Tegular 2x2 Primed White With Backer 1/16" | 0' - 0" | Yes | 0 | 0' - 0" | 1 | Paint - Acoustical-Surfaces - Primed White | 2' - 0" | 0' - 1" | 1 | Yes | No | No | Yes | No | No | No | Yes | No |
| 1" Tegular 2x4 Primed Clear With Backer 1/16" | 0' - 0" | Yes | 0 | 0' - 0" | 1 | Paint - Acoustical-Surfaces - Primed Clear | 4' - 0" | 0' - 1" | 1 | Yes | No | No | Yes | No | No | No | Yes | No |
| 1" Tegular 2x2 Primed Clear With Backer 1/16" | 0' - 0" | Yes | 0 | 0' - 0" | 1 | Paint - Acoustical-Surfaces - Primed Clear | 2' - 0" | 0' - 1" | 1 | Yes | No | No | Yes | No | No | No | Yes | No |

## geometry (parser evidence)
native form markers: Sweep x10
no freeform markers — native parametric forms only
